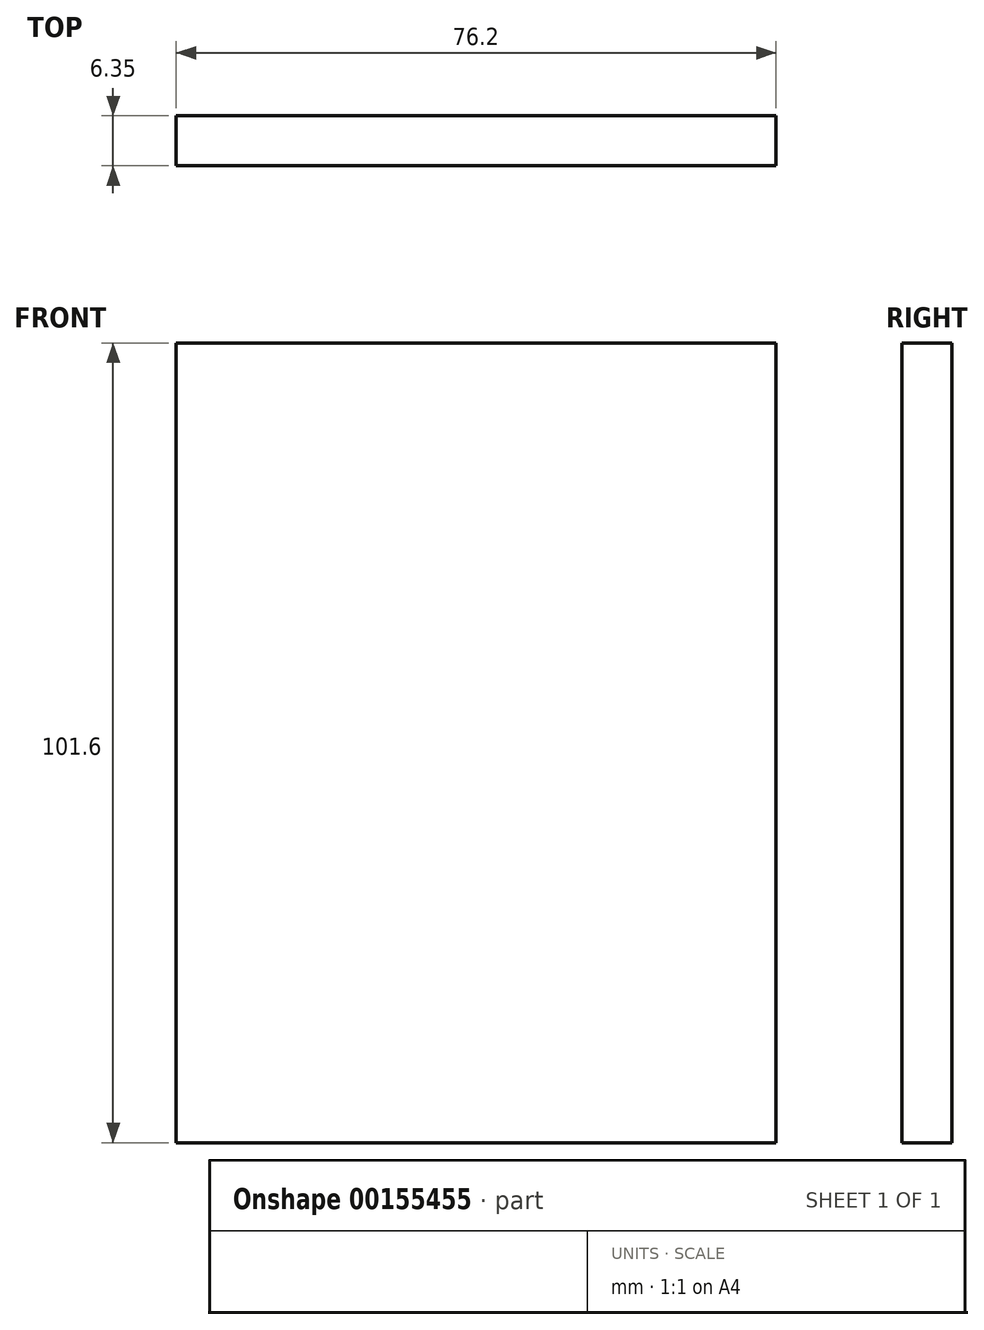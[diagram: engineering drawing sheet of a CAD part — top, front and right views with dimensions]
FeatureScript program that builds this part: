
annotation { "Feature Type Name" : "Feature", "Feature Type Description" : "" }
export const myFeature = defineFeature(function(context is Context, id is Id, definition is map)
    precondition{}
    {
        {
            var Q0;
            Q0=qCreatedBy(makeId("Front.planeOp"),FACE);
            var sketch = newSketch(context, id + "F0", { "sketchPlane" : qUnion([Q0])});
            skLineSegment(sketch, "E0.bottom", {"start": v(0, 0) * mm, "end": v(76.2, 0) * mm});
            skLineSegment(sketch, "E0.top", {"start": v(0, -101.6) * mm, "end": v(76.2, -101.6) * mm});
            skLineSegment(sketch, "E0.left", {"start": v(0, 0) * mm, "end": v(0, -101.6) * mm});
            skLineSegment(sketch, "E0.right", {"start": v(76.2, 0) * mm, "end": v(76.2, -101.6) * mm});
            skSolve(sketch);
        }
        {
            var Q0;
            Q0 = qSketchRegion(id + "F0", true);
            extrude(context, id + "F1", {"entities" : qUnion([Q0]), "depth" : 6.35 * mm});
        }
    });
